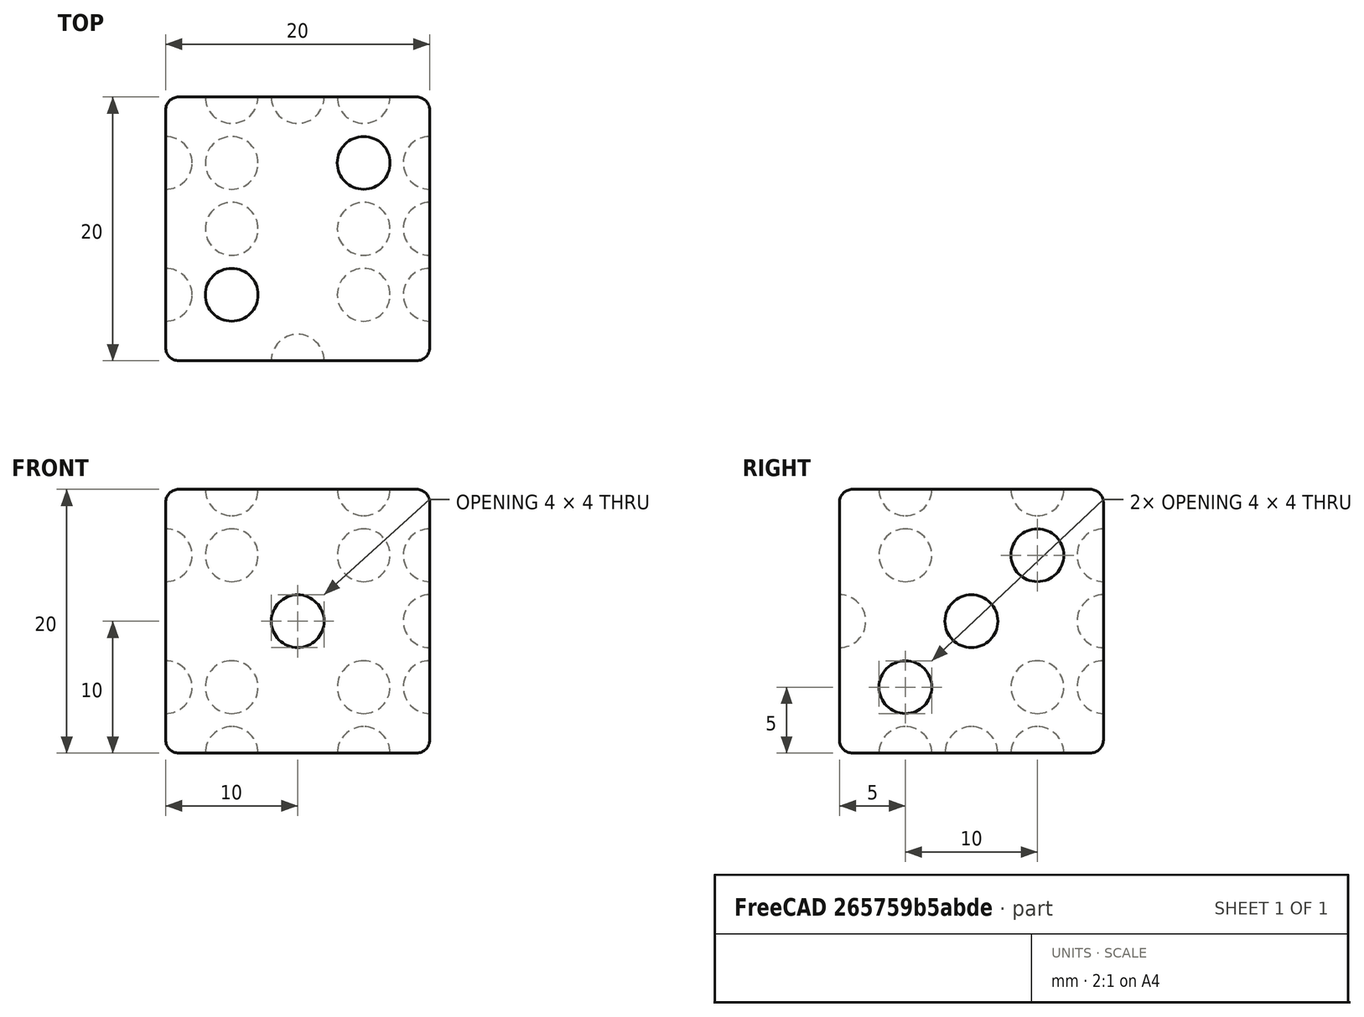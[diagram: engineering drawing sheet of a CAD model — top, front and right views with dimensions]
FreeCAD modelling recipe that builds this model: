
FCSTD DOCUMENT  (FreeCAD 0.18R4 (GitTag))
Label: 13_dado
License: All rights reserved
LicenseURL: http://en.wikipedia.org/wiki/All_rights_reserved
objects: Part::Sphere×21, Part::MultiFuse×6, Part::Box×1, Part::Fillet×1, Part::Cut×1
note: 30 computed .brp shape members not serialized (recipe doc carries the construction recipe); baked Part::Feature solids carry a one-line shape summary decoded from their .brp

FEATURE [Part::Box] Box  label="dado_base"
  AttacherType = Attacher::AttachEngine3D
  Height = 20
  Length = 20
  Width = 20
FEATURE [Part::Fillet] Fillet  label="dado_base_redondeado"
  Base = -> Box
  Edges = 12 edges r=1: [Edge1,Edge2,Edge3,Edge4,Edge5,Edge6,Edge7,Edge8,Edge9,Edge10,Edge11,Edge12]
FEATURE [Part::Sphere] Sphere  label="uno"
  Angle1 = -90
  Angle2 = 90
  Angle3 = 360
  AttacherType = Attacher::AttachEngine3D
  Placement = pos=(10,0,10) rot=(0,0,1;0rad)
  Radius = 2
FEATURE [Part::Sphere] Sphere001  label="tres_1"
  Angle1 = -90
  Angle2 = 90
  Angle3 = 360
  AttacherType = Attacher::AttachEngine3D
  Placement = pos=(20,10,10) rot=(0,0,1;0rad)
  Radius = 2
FEATURE [Part::Sphere] Sphere002  label="tres_2"
  Angle1 = -90
  Angle2 = 90
  Angle3 = 360
  AttacherType = Attacher::AttachEngine3D
  Placement = pos=(20,5,5) rot=(0,0,1;0rad)
  Radius = 2
FEATURE [Part::Sphere] Sphere003  label="tres_3"
  Angle1 = -90
  Angle2 = 90
  Angle3 = 360
  AttacherType = Attacher::AttachEngine3D
  Placement = pos=(20,15,15) rot=(0,0,1;0rad)
  Radius = 2
FEATURE [Part::MultiFuse] Fusion  label="tres"
  Refine = true
  Shapes = -> [Sphere003,Sphere001,Sphere002]
FEATURE [Part::Sphere] Sphere004  label="dos_1"
  Angle1 = -90
  Angle2 = 90
  Angle3 = 360
  AttacherType = Attacher::AttachEngine3D
  Placement = pos=(15,15,20) rot=(0,0,1;0rad)
  Radius = 2
FEATURE [Part::Sphere] Sphere006  label="dos_2"
  Angle1 = -90
  Angle2 = 90
  Angle3 = 360
  AttacherType = Attacher::AttachEngine3D
  Placement = pos=(5,5,20) rot=(0,0,1;0rad)
  Radius = 2
FEATURE [Part::MultiFuse] Fusion001  label="dos"
  Refine = true
  Shapes = -> [Sphere006,Sphere004]
FEATURE [Part::Sphere] Sphere007  label="cinco_1"
  Angle1 = -90
  Angle2 = 90
  Angle3 = 360
  AttacherType = Attacher::AttachEngine3D
  Placement = pos=(15,20,15) rot=(0,0,1;0rad)
  Radius = 2
FEATURE [Part::Sphere] Sphere008  label="cinco_2"
  Angle1 = -90
  Angle2 = 90
  Angle3 = 360
  AttacherType = Attacher::AttachEngine3D
  Placement = pos=(10,20,10) rot=(0,0,1;0rad)
  Radius = 2
FEATURE [Part::Sphere] Sphere009  label="cinco_3"
  Angle1 = -90
  Angle2 = 90
  Angle3 = 360
  AttacherType = Attacher::AttachEngine3D
  Placement = pos=(5,20,5) rot=(0,0,1;0rad)
  Radius = 2
FEATURE [Part::Sphere] Sphere010  label="cinco_4"
  Angle1 = -90
  Angle2 = 90
  Angle3 = 360
  AttacherType = Attacher::AttachEngine3D
  Placement = pos=(5,20,15) rot=(0,0,1;0rad)
  Radius = 2
FEATURE [Part::Sphere] Sphere011  label="cinco_5"
  Angle1 = -90
  Angle2 = 90
  Angle3 = 360
  AttacherType = Attacher::AttachEngine3D
  Placement = pos=(15,20,5) rot=(0,0,1;0rad)
  Radius = 2
FEATURE [Part::MultiFuse] Fusion002  label="cinco"
  Refine = true
  Shapes = -> [Sphere007,Sphere009,Sphere008,Sphere010,Sphere011]
FEATURE [Part::Sphere] Sphere012  label="cuatro_2"
  Angle1 = -90
  Angle2 = 90
  Angle3 = 360
  AttacherType = Attacher::AttachEngine3D
  Placement = pos=(0,15,15) rot=(0,0,1;0rad)
  Radius = 2
FEATURE [Part::Sphere] Sphere013  label="cuatro_1"
  Angle1 = -90
  Angle2 = 90
  Angle3 = 360
  AttacherType = Attacher::AttachEngine3D
  Placement = pos=(0,5,15) rot=(0,0,1;0rad)
  Radius = 2
FEATURE [Part::Sphere] Sphere014  label="cuatro_3"
  Angle1 = -90
  Angle2 = 90
  Angle3 = 360
  AttacherType = Attacher::AttachEngine3D
  Placement = pos=(0,15,5) rot=(0,0,1;0rad)
  Radius = 2
FEATURE [Part::Sphere] Sphere015  label="cuatro_4"
  Angle1 = -90
  Angle2 = 90
  Angle3 = 360
  AttacherType = Attacher::AttachEngine3D
  Placement = pos=(0,5,5) rot=(0,0,1;0rad)
  Radius = 2
FEATURE [Part::MultiFuse] Fusion003  label="cuatro"
  Refine = true
  Shapes = -> [Sphere015,Sphere014,Sphere013,Sphere012]
FEATURE [Part::Sphere] Sphere016  label="seis_2"
  Angle1 = -90
  Angle2 = 90
  Angle3 = 360
  AttacherType = Attacher::AttachEngine3D
  Placement = pos=(5,15,0) rot=(0,0,1;0rad)
  Radius = 2
FEATURE [Part::Sphere] Sphere017  label="seis_3"
  Angle1 = -90
  Angle2 = 90
  Angle3 = 360
  AttacherType = Attacher::AttachEngine3D
  Placement = pos=(15,5,0) rot=(0,0,1;0rad)
  Radius = 2
FEATURE [Part::Sphere] Sphere018  label="seis_1"
  Angle1 = -90
  Angle2 = 90
  Angle3 = 360
  AttacherType = Attacher::AttachEngine3D
  Placement = pos=(5,5,0) rot=(0,0,1;0rad)
  Radius = 2
FEATURE [Part::Sphere] Sphere019  label="seis_4"
  Angle1 = -90
  Angle2 = 90
  Angle3 = 360
  AttacherType = Attacher::AttachEngine3D
  Placement = pos=(15,15,0) rot=(0,0,1;0rad)
  Radius = 2
FEATURE [Part::Sphere] Sphere020  label="seis_5"
  Angle1 = -90
  Angle2 = 90
  Angle3 = 360
  AttacherType = Attacher::AttachEngine3D
  Placement = pos=(5,10,0) rot=(0,0,1;0rad)
  Radius = 2
FEATURE [Part::Sphere] Sphere021  label="seis_6"
  Angle1 = -90
  Angle2 = 90
  Angle3 = 360
  AttacherType = Attacher::AttachEngine3D
  Placement = pos=(15,10,0) rot=(0,0,1;0rad)
  Radius = 2
FEATURE [Part::MultiFuse] Fusion004  label="seis"
  Refine = true
  Shapes = -> [Sphere018,Sphere020,Sphere019,Sphere021,Sphere017,Sphere016]
FEATURE [Part::MultiFuse] Fusion005  label="numeros"
  Refine = true
  Shapes = -> [Fusion004,Fusion002,Fusion001,Fusion003,Fusion,Sphere]
FEATURE [Part::Cut] Cut  label="dado"
  Base = -> Fillet
  Refine = true
  Tool = -> Fusion005
